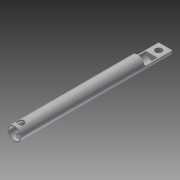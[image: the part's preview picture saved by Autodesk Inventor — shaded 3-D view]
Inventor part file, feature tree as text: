
AUTODESK INVENTOR PART (.ipt)
format: ipt  version: 2013 (Build 170138000, 138)  size: 158,208 bytes
history: native  units: in
note: dims shown in document units (in); Inventor stores cm internally (conversion verified against a paired STEP export)
features: sketch x8, extrude x7, plane x5, fillet x2
ambient origin geometry x8: Origin, YZ Plane, XZ Plane, XY Plane, X Axis, Y Axis, Z Axis, Center Point
bodies: Solid1 (feature_tree)
feature tree (22):
  extrude  "Extrusion1"  Depth=0.85in
  plane  "Work Plane2"
  extrude  "Extrusion2"  Depth=0.5in TaperAngle=90.0deg
  sketch  "Sketch3"  dims[d6=11.0in d7=0.45in]
  plane  "Work Plane4"
  extrude  "Extrusion3"  Depth=0.45in
  extrude  "Extrusion4"  Depth=0.55in
  extrude  "Extrusion5"  Depth=11.0in TaperAngle=0.0deg
  extrude  "Extrusion6"  Depth=1.5in
  fillet  "Fillet1"  Radius=2.0in
  plane  "Work Plane5"
  extrude  "Extrusion7"  Depth=0.5in TaperAngle=0.0deg
  fillet  "Fillet2"  Radius=0.5in
  sketch  "Sketch1"  dims[d0=1.0in d1=0.85in]
  plane  "Work Plane1"
  sketch  "Sketch2"  dims[d2=11.0in d3=0.0in d4=90.0deg d5=0.5in]
  plane  "Work Plane3"
  sketch  "Sketch4"  dims[d8=0.5in d9=0.55in]
  sketch  "Sketch5"  dims[d10=0.5in d11=11.0in d12=0.0in]
  sketch  "Sketch6"  dims[d13=90.0deg d14=0.5in d15=1.5in d16=2.0in d17=0.0in]
  sketch  "Sketch7"  dims[d18=1.0in d19=0.5in d20=0.0in d21=0.5in]
  sketch  "Sketch8"  dims[d22=0.5in d23=0.0in d24=15.0in d25=0.0in d26=0.125in d27=90.0deg d28=0.65in d29=15.0in d30=0.0in d31=0.125in]
